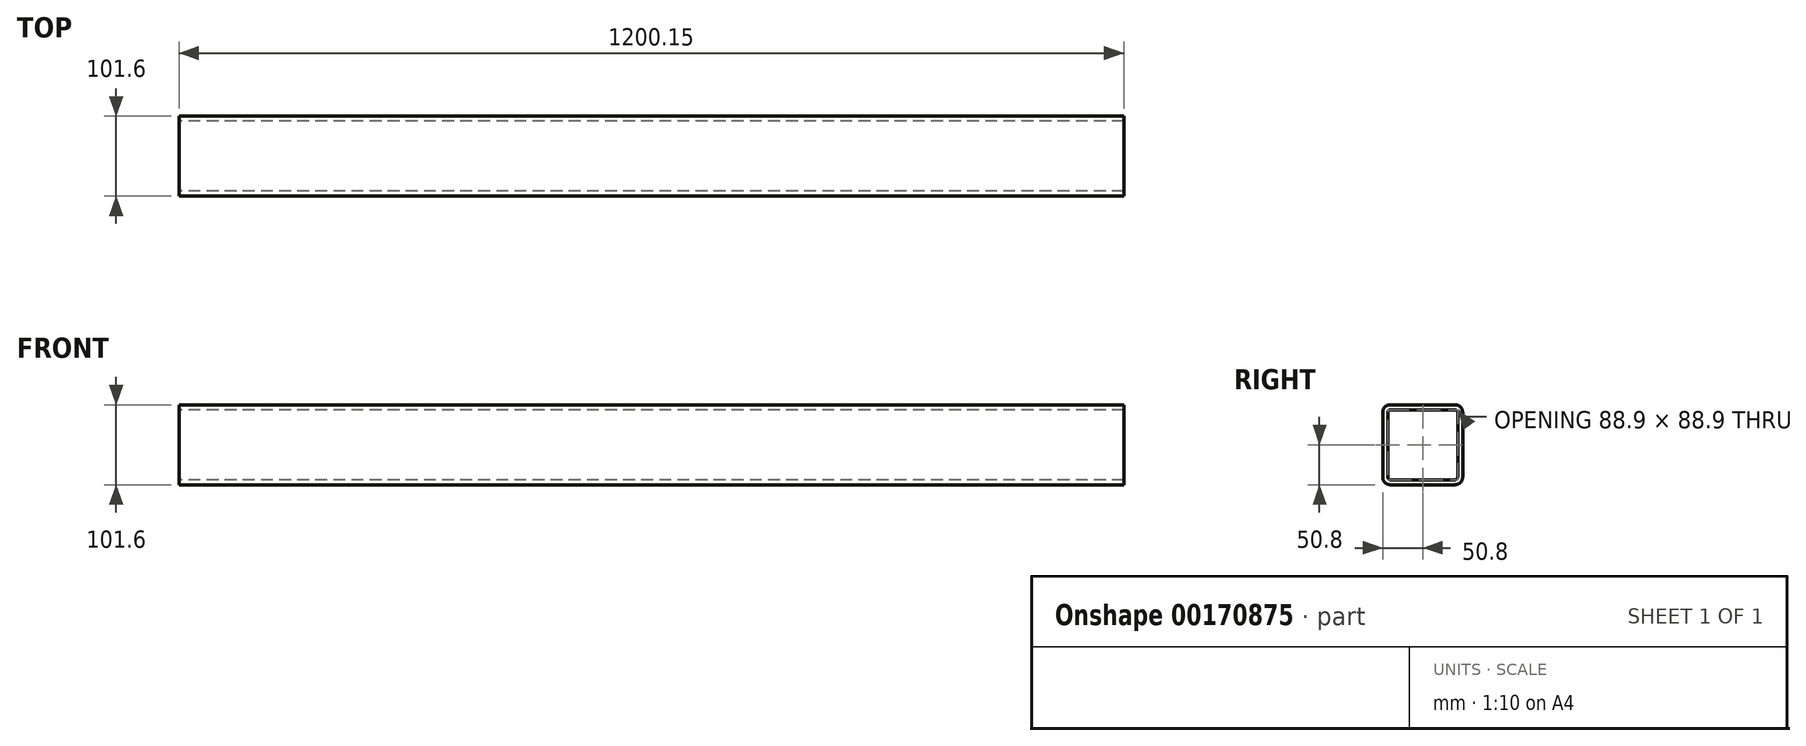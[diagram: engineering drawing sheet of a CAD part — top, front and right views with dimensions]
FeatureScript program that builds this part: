
annotation { "Feature Type Name" : "Feature", "Feature Type Description" : "" }
export const myFeature = defineFeature(function(context is Context, id is Id, definition is map)
    precondition{}
    {
        {
            var Q0;
            Q0=qCreatedBy(makeId("Right.planeOp"),FACE);
            var sketch = newSketch(context, id + "F0", { "sketchPlane" : qUnion([Q0])});
            skLineSegment(sketch, "E0.bottom", {"start": v(9.52, 0) * mm, "end": v(92.08, 0) * mm});
            skLineSegment(sketch, "E0.top", {"start": v(9.52, 101.6) * mm, "end": v(92.08, 101.6) * mm});
            skLineSegment(sketch, "E0.left", {"start": v(0, 9.52) * mm, "end": v(0, 92.07) * mm});
            skLineSegment(sketch, "E0.right", {"start": v(101.6, 9.52) * mm, "end": v(101.6, 92.07) * mm});
            skPoint(sketch, "E1.visualSharp", {"position": v(101.6, 101.6) * mm});
            skArc(sketch, "E1.filletArc", {"start": v(101.6, 92.07) * mm, "mid": v(98.81, 98.81) * mm, "end": v(92.08, 101.6) * mm});
            skPoint(sketch, "E2.visualSharp", {"position": v(101.6, 0) * mm});
            skArc(sketch, "E2.filletArc", {"start": v(92.08, 0) * mm, "mid": v(98.81, 2.79) * mm, "end": v(101.6, 9.52) * mm});
            skPoint(sketch, "E3.visualSharp", {"position": v(0, 0) * mm});
            skArc(sketch, "E3.filletArc", {"start": v(0, 9.52) * mm, "mid": v(2.79, 2.79) * mm, "end": v(9.52, 0) * mm});
            skPoint(sketch, "E4.visualSharp", {"position": v(0, 101.6) * mm});
            skArc(sketch, "E4.filletArc", {"start": v(9.52, 101.6) * mm, "mid": v(2.79, 98.81) * mm, "end": v(0, 92.07) * mm});
            skArc(sketch, "E5.0", {"start": v(92.08, 6.35) * mm, "mid": v(94.32, 7.28) * mm, "end": v(95.25, 9.53) * mm});
            skLineSegment(sketch, "E5.1", {"start": v(9.52, 6.35) * mm, "end": v(92.08, 6.35) * mm});
            skLineSegment(sketch, "E5.2", {"start": v(95.25, 9.52) * mm, "end": v(95.25, 92.07) * mm});
            skArc(sketch, "E5.3", {"start": v(6.35, 9.53) * mm, "mid": v(7.28, 7.28) * mm, "end": v(9.52, 6.35) * mm});
            skArc(sketch, "E5.4", {"start": v(95.25, 92.07) * mm, "mid": v(94.32, 94.32) * mm, "end": v(92.07, 95.25) * mm});
            skLineSegment(sketch, "E5.5", {"start": v(9.52, 95.25) * mm, "end": v(92.07, 95.25) * mm});
            skArc(sketch, "E5.6", {"start": v(9.52, 95.25) * mm, "mid": v(7.28, 94.32) * mm, "end": v(6.35, 92.07) * mm});
            skLineSegment(sketch, "E5.7", {"start": v(6.35, 9.52) * mm, "end": v(6.35, 92.07) * mm});
            skSolve(sketch);
        }
        {
            var Q0;
            Q0 = qSketchRegion(id + "F0", true);
            extrude(context, id + "F1", {"entities" : qUnion([Q0]), "depth" : 1200.15 * mm, "offsetDistance" : 25.4 * mm});
        }
    });
